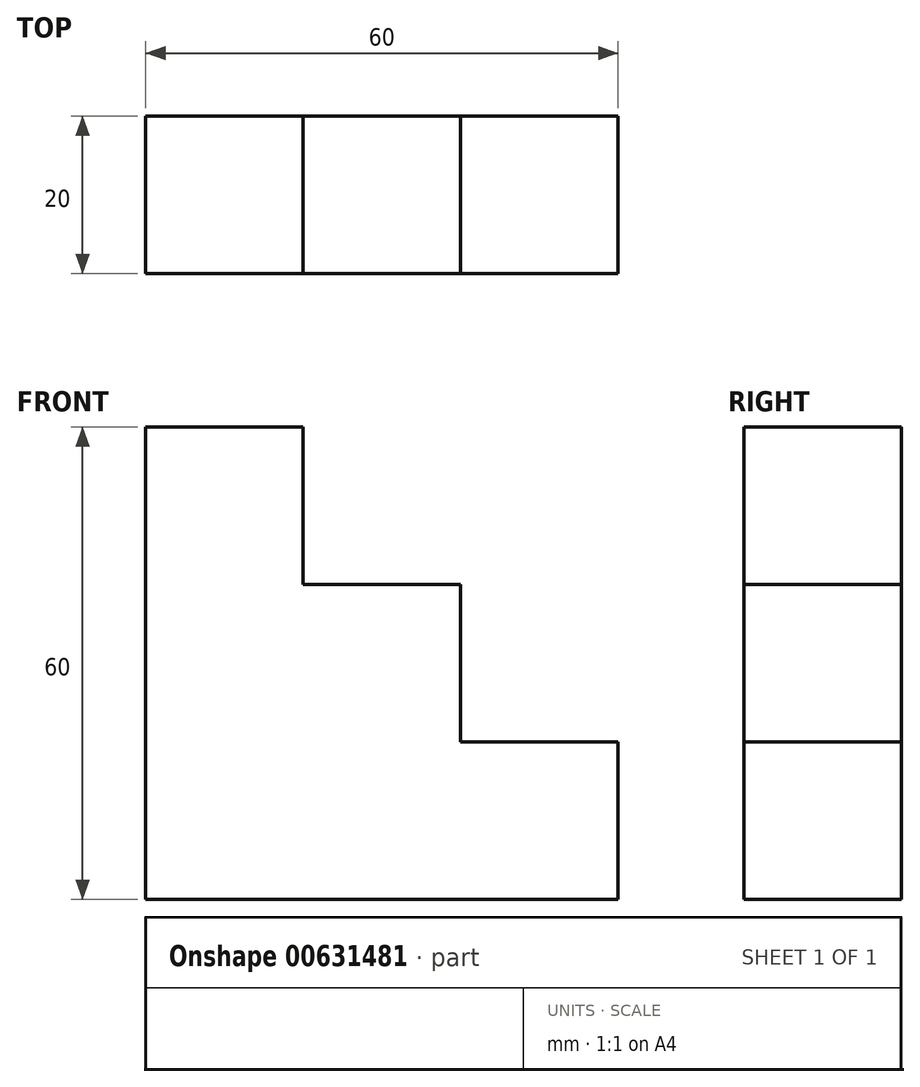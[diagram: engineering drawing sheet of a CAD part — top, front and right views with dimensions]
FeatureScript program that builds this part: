
annotation { "Feature Type Name" : "Feature", "Feature Type Description" : "" }
export const myFeature = defineFeature(function(context is Context, id is Id, definition is map)
    precondition{}
    {
        {
            var Q0;
            Q0=qCreatedBy(makeId("Front.planeOp"),FACE);
            var sketch = newSketch(context, id + "F0", { "sketchPlane" : qUnion([Q0])});
            skLineSegment(sketch, "E0", {"start": v(-15.85, 40) * mm, "end": v(-15.85, -20) * mm});
            skLineSegment(sketch, "E1", {"start": v(-15.85, -20) * mm, "end": v(44.15, -20) * mm});
            skLineSegment(sketch, "E2", {"start": v(44.15, -20) * mm, "end": v(44.15, 0) * mm});
            skLineSegment(sketch, "E3", {"start": v(44.15, 0) * mm, "end": v(24.15, 0) * mm});
            skLineSegment(sketch, "E4", {"start": v(24.15, 0) * mm, "end": v(24.15, 20) * mm});
            skLineSegment(sketch, "E5", {"start": v(24.15, 20) * mm, "end": v(4.15, 20) * mm});
            skLineSegment(sketch, "E6", {"start": v(4.15, 20) * mm, "end": v(4.15, 40) * mm});
            skLineSegment(sketch, "E7", {"start": v(4.15, 40) * mm, "end": v(-15.85, 40) * mm});
            skSolve(sketch);
        }
        {
            var Q0;
            Q0 = qSketchRegion(id + "F0", true);
            extrude(context, id + "F1", {"entities" : qUnion([Q0]), "depth" : 20 * mm, "offsetDistance" : 25 * mm});
        }
    });
